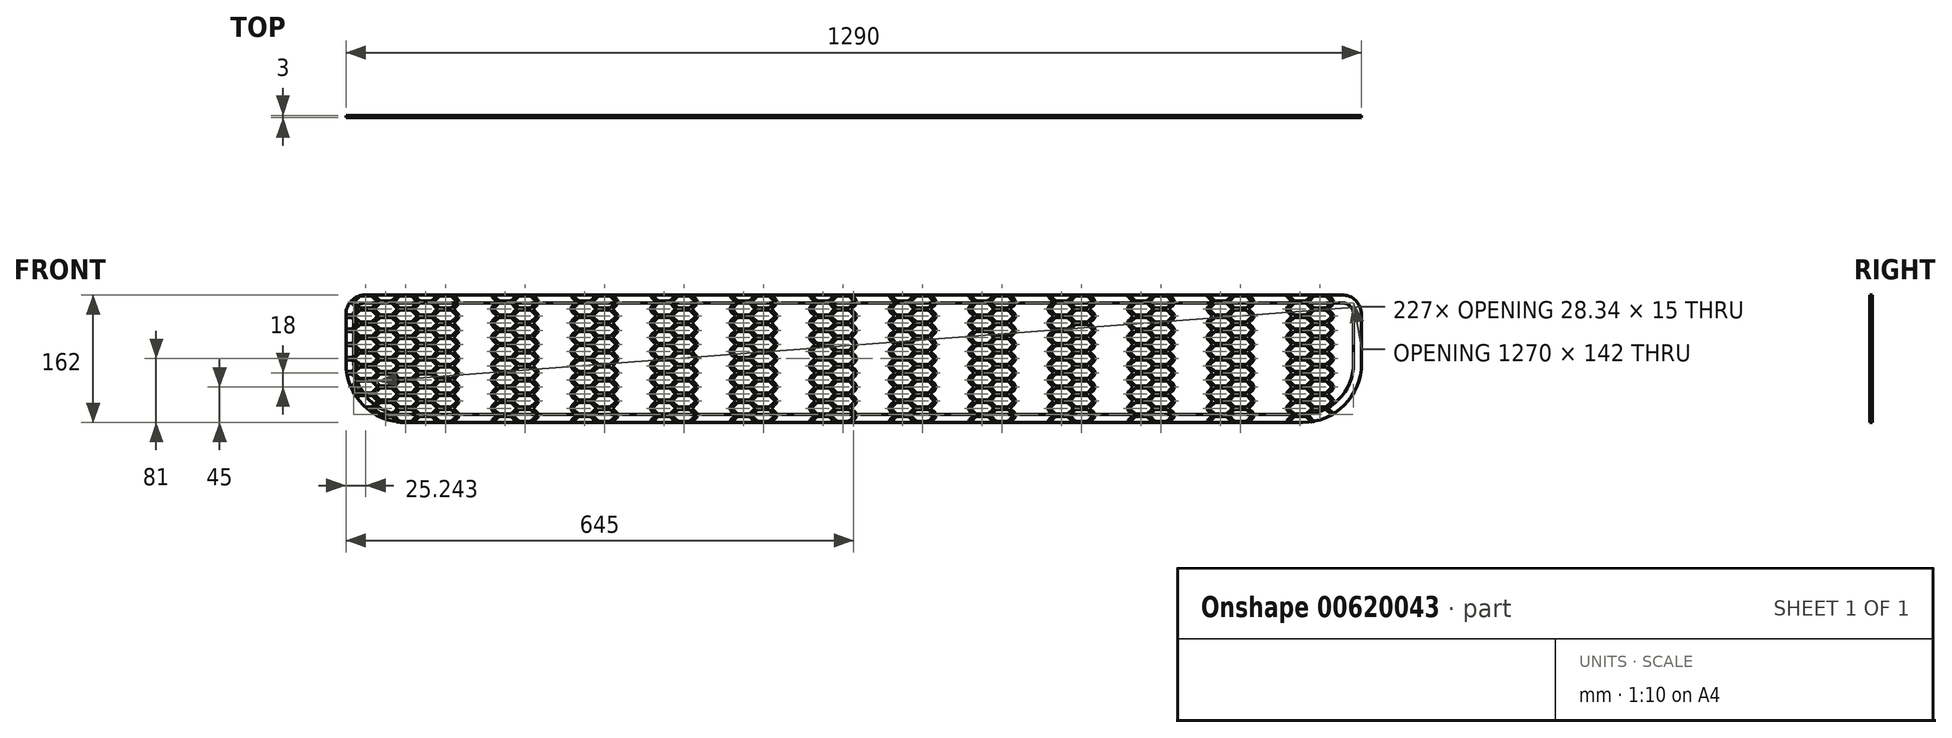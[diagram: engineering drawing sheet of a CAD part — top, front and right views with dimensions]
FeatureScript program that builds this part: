
annotation { "Feature Type Name" : "Feature", "Feature Type Description" : "" }
export const myFeature = defineFeature(function(context is Context, id is Id, definition is map)
    precondition{}
    {
        {
            var Q0;
            Q0=qCreatedBy(makeId("Front.planeOp"),FACE);
            var sketch = newSketch(context, id + "F0", { "sketchPlane" : qUnion([Q0])});
            skLineSegment(sketch, "E0.bottom", {"start": v(6.67, -7.5) * mm, "end": v(-6.67, -7.5) * mm});
            skLineSegment(sketch, "E0.top", {"start": v(6.67, 7.5) * mm, "end": v(-6.67, 7.5) * mm});
            skPoint(sketch, "E0.middle", {"position": v(0, 0) * mm});
            skLineSegment(sketch, "E1", {"start": v(-8.09, 6.91) * mm, "end": v(-13.59, 1.41) * mm});
            skLineSegment(sketch, "E2", {"start": v(-8.09, -6.91) * mm, "end": v(-13.59, -1.41) * mm});
            skLineSegment(sketch, "E3", {"start": v(8.09, 6.91) * mm, "end": v(13.59, 1.41) * mm});
            skLineSegment(sketch, "E4", {"start": v(13.59, -1.41) * mm, "end": v(8.09, -6.91) * mm});
            skPoint(sketch, "E5.visualSharp", {"position": v(-15, 0) * mm});
            skArc(sketch, "E5.filletArc", {"start": v(-13.59, 1.41) * mm, "mid": v(-14.17, 0) * mm, "end": v(-13.59, -1.41) * mm});
            skPoint(sketch, "E6.visualSharp", {"position": v(15, 0) * mm});
            skArc(sketch, "E6.filletArc", {"start": v(13.59, -1.41) * mm, "mid": v(14.17, 0) * mm, "end": v(13.59, 1.41) * mm});
            skPoint(sketch, "E7.visualSharp", {"position": v(7.5, -7.5) * mm});
            skArc(sketch, "E7.filletArc", {"start": v(6.67, -7.5) * mm, "mid": v(7.44, -7.35) * mm, "end": v(8.09, -6.91) * mm});
            skPoint(sketch, "E8.visualSharp", {"position": v(-7.5, -7.5) * mm});
            skArc(sketch, "E8.filletArc", {"start": v(-8.09, -6.91) * mm, "mid": v(-7.44, -7.35) * mm, "end": v(-6.67, -7.5) * mm});
            skArc(sketch, "E9.filletArc", {"start": v(-6.67, 7.5) * mm, "mid": v(-7.44, 7.35) * mm, "end": v(-8.09, 6.91) * mm});
            skArc(sketch, "E10.filletArc", {"start": v(8.09, 6.91) * mm, "mid": v(7.44, 7.35) * mm, "end": v(6.67, 7.5) * mm});
            skLineSegment(sketch, "E11.0.7.2", {"start": v(17.16, 160.1) * mm, "end": v(11.66, 154.6) * mm});
            skLineSegment(sketch, "E11.0.7.3", {"start": v(31.91, 160.68) * mm, "end": v(18.57, 160.68) * mm});
            skLineSegment(sketch, "E11.0.7.5", {"start": v(33.33, 160.1) * mm, "end": v(38.83, 154.6) * mm});
            skArc(sketch, "E11.0.7.7", {"start": v(33.33, 160.1) * mm, "mid": v(32.68, 160.53) * mm, "end": v(31.91, 160.68) * mm});
            skArc(sketch, "E11.0.7.10", {"start": v(18.57, 160.68) * mm, "mid": v(17.8, 160.53) * mm, "end": v(17.16, 160.1) * mm});
            skArc(sketch, "E12.0", {"start": v(10.2, 9.04) * mm, "mid": v(8.58, 10.12) * mm, "end": v(6.67, 10.5) * mm});
            skLineSegment(sketch, "E12.1", {"start": v(-10.2, -9.04) * mm, "end": v(-15.7, -3.54) * mm});
            skArc(sketch, "E12.2", {"start": v(-15.7, 3.54) * mm, "mid": v(-17.17, 0) * mm, "end": v(-15.7, -3.54) * mm});
            skLineSegment(sketch, "E12.3", {"start": v(-10.2, 9.04) * mm, "end": v(-15.7, 3.54) * mm});
            skArc(sketch, "E12.4", {"start": v(-6.67, 10.5) * mm, "mid": v(-8.58, 10.12) * mm, "end": v(-10.2, 9.04) * mm});
            skArc(sketch, "E12.5", {"start": v(-10.2, -9.04) * mm, "mid": v(-8.58, -10.12) * mm, "end": v(-6.67, -10.5) * mm});
            skLineSegment(sketch, "E12.6", {"start": v(6.67, 10.5) * mm, "end": v(-6.67, 10.5) * mm});
            skLineSegment(sketch, "E12.7", {"start": v(6.67, -10.5) * mm, "end": v(-6.67, -10.5) * mm});
            skArc(sketch, "E12.8", {"start": v(6.67, -10.5) * mm, "mid": v(8.58, -10.12) * mm, "end": v(10.2, -9.04) * mm});
            skLineSegment(sketch, "E12.9", {"start": v(15.7, -3.54) * mm, "end": v(10.2, -9.04) * mm});
            skArc(sketch, "E12.10", {"start": v(15.7, -3.54) * mm, "mid": v(17.17, 0) * mm, "end": v(15.7, 3.54) * mm});
            skLineSegment(sketch, "E12.11", {"start": v(10.2, 9.04) * mm, "end": v(15.7, 3.54) * mm});
            skLineSegment(sketch, "E13.bottom", {"start": v(-6.67, 5.5) * mm, "end": v(6.67, 5.5) * mm, "construction": true});
            skLineSegment(sketch, "E13.top", {"start": v(-6.67, -5.5) * mm, "end": v(6.67, -5.5) * mm, "construction": true});
            skLineSegment(sketch, "E13.left", {"start": v(-6.67, 5.5) * mm, "end": v(-6.67, -5.5) * mm, "construction": true});
            skLineSegment(sketch, "E13.right", {"start": v(6.67, 5.5) * mm, "end": v(6.67, -5.5) * mm, "construction": true});
            skSolve(sketch);
        }
        {
            var Q0;
            Q0=makeQuery(id+"F0.imprint","IMPRINT",FACE,{"disambiguationData":[TD([[makeQuery(id+"F0.imprint","IMPRINT",EDGE,{"derivedFrom":sQuery(id+"F0.wireOp",EDGE,"E0.bottom")}),1.0]])]});
            extrude(context, id + "F1", {"entities" : qUnion([Q0]), "depth" : 3 * mm, "offsetDistance" : 25 * mm});
        }
        {
            var Q0;
            Q0=qCreatedBy(makeId("Front.planeOp"),FACE);
            var sketch = newSketch(context, id + "F2", { "sketchPlane" : qUnion([Q0])});
            skLineSegment(sketch, "E14.0", {"start": v(6.67, -7.5) * mm, "end": v(-6.67, -7.5) * mm});
            skLineSegment(sketch, "E15.bottom", {"start": v(6.67, -25.5) * mm, "end": v(-6.67, -25.5) * mm});
            skLineSegment(sketch, "E15.top", {"start": v(6.67, -10.5) * mm, "end": v(-6.67, -10.5) * mm});
            skPoint(sketch, "E15.middle", {"position": v(0, -18) * mm});
            skLineSegment(sketch, "E16", {"start": v(-8.09, -11.09) * mm, "end": v(-13.59, -16.59) * mm});
            skLineSegment(sketch, "E17", {"start": v(-8.09, -24.91) * mm, "end": v(-13.59, -19.41) * mm});
            skLineSegment(sketch, "E18", {"start": v(8.09, -11.09) * mm, "end": v(13.59, -16.59) * mm});
            skLineSegment(sketch, "E19", {"start": v(13.59, -19.41) * mm, "end": v(8.09, -24.91) * mm});
            skPoint(sketch, "E20.visualSharp", {"position": v(-15, -18) * mm});
            skArc(sketch, "E20.filletArc", {"start": v(-13.59, -16.59) * mm, "mid": v(-14.17, -18) * mm, "end": v(-13.59, -19.41) * mm});
            skPoint(sketch, "E21.visualSharp", {"position": v(15, -18) * mm});
            skArc(sketch, "E21.filletArc", {"start": v(13.59, -19.41) * mm, "mid": v(14.17, -18) * mm, "end": v(13.59, -16.59) * mm});
            skPoint(sketch, "E22.visualSharp", {"position": v(7.5, -25.5) * mm});
            skArc(sketch, "E22.filletArc", {"start": v(6.67, -25.5) * mm, "mid": v(7.44, -25.35) * mm, "end": v(8.09, -24.91) * mm});
            skPoint(sketch, "E23.visualSharp", {"position": v(-7.5, -25.5) * mm});
            skArc(sketch, "E23.filletArc", {"start": v(-8.09, -24.91) * mm, "mid": v(-7.44, -25.35) * mm, "end": v(-6.67, -25.5) * mm});
            skArc(sketch, "E24.filletArc", {"start": v(-6.67, -10.5) * mm, "mid": v(-7.44, -10.65) * mm, "end": v(-8.09, -11.09) * mm});
            skArc(sketch, "E25.filletArc", {"start": v(8.09, -11.09) * mm, "mid": v(7.44, -10.65) * mm, "end": v(6.67, -10.5) * mm});
            skArc(sketch, "E26.0", {"start": v(10.2, -8.96) * mm, "mid": v(8.58, -7.88) * mm, "end": v(6.67, -7.5) * mm});
            skLineSegment(sketch, "E26.1", {"start": v(-10.2, -27.04) * mm, "end": v(-15.7, -21.54) * mm});
            skArc(sketch, "E26.2", {"start": v(-15.7, -14.46) * mm, "mid": v(-17.17, -18) * mm, "end": v(-15.7, -21.54) * mm});
            skLineSegment(sketch, "E26.3", {"start": v(-10.2, -8.96) * mm, "end": v(-15.7, -14.46) * mm});
            skArc(sketch, "E26.4", {"start": v(-6.67, -7.5) * mm, "mid": v(-8.58, -7.88) * mm, "end": v(-10.2, -8.96) * mm});
            skArc(sketch, "E26.5", {"start": v(-10.2, -27.04) * mm, "mid": v(-8.58, -28.12) * mm, "end": v(-6.67, -28.5) * mm});
            skLineSegment(sketch, "E26.7", {"start": v(6.67, -28.5) * mm, "end": v(-6.67, -28.5) * mm});
            skArc(sketch, "E26.8", {"start": v(6.67, -28.5) * mm, "mid": v(8.58, -28.12) * mm, "end": v(10.2, -27.04) * mm});
            skLineSegment(sketch, "E26.9", {"start": v(15.7, -21.54) * mm, "end": v(10.2, -27.04) * mm});
            skArc(sketch, "E26.10", {"start": v(15.7, -21.54) * mm, "mid": v(17.17, -18) * mm, "end": v(15.7, -14.46) * mm});
            skLineSegment(sketch, "E26.11", {"start": v(10.2, -8.96) * mm, "end": v(15.7, -14.46) * mm});
            skLineSegment(sketch, "E27.bottom", {"start": v(-6.67, -12.5) * mm, "end": v(6.67, -12.5) * mm, "construction": true});
            skLineSegment(sketch, "E27.top", {"start": v(-6.67, -23.5) * mm, "end": v(6.67, -23.5) * mm, "construction": true});
            skLineSegment(sketch, "E27.left", {"start": v(-6.67, -12.5) * mm, "end": v(-6.67, -23.5) * mm, "construction": true});
            skLineSegment(sketch, "E27.right", {"start": v(6.67, -12.5) * mm, "end": v(6.67, -23.5) * mm, "construction": true});
            skSolve(sketch);
        }
        {
            var Q0;
            Q0=makeQuery(id+"F2.imprint","IMPRINT",FACE,{"disambiguationData":[TD([[makeQuery(id+"F2.imprint","IMPRINT",EDGE,{"derivedFrom":sQuery(id+"F2.wireOp",EDGE,"E15.bottom")}),1.0]])]});
            extrude(context, id + "F3", {"entities" : qUnion([Q0]), "operationType" : NewBodyOperationType.ADD, "depth" : 3 * mm, "offsetDistance" : 25 * mm});
        }
        {
            var Q0;
            Q0=qCreatedBy(makeId("Front.planeOp"),FACE);
            var sketch = newSketch(context, id + "F4", { "sketchPlane" : qUnion([Q0])});
            skLineSegment(sketch, "E28.bottom", {"start": v(64.28, 40.04) * mm, "end": v(50.94, 40.04) * mm});
            skLineSegment(sketch, "E28.top", {"start": v(64.28, 55.04) * mm, "end": v(50.94, 55.04) * mm});
            skPoint(sketch, "E28.middle", {"position": v(57.61, 47.54) * mm});
            skLineSegment(sketch, "E29", {"start": v(49.53, 54.45) * mm, "end": v(44.03, 48.95) * mm});
            skLineSegment(sketch, "E30", {"start": v(49.53, 40.62) * mm, "end": v(44.03, 46.12) * mm});
            skLineSegment(sketch, "E31", {"start": v(65.7, 54.45) * mm, "end": v(71.2, 48.95) * mm});
            skLineSegment(sketch, "E32", {"start": v(71.2, 46.12) * mm, "end": v(65.7, 40.62) * mm});
            skPoint(sketch, "E33.visualSharp", {"position": v(42.61, 47.54) * mm});
            skArc(sketch, "E33.filletArc", {"start": v(44.03, 48.95) * mm, "mid": v(43.44, 47.54) * mm, "end": v(44.03, 46.12) * mm});
            skPoint(sketch, "E34.visualSharp", {"position": v(72.61, 47.54) * mm});
            skArc(sketch, "E34.filletArc", {"start": v(71.2, 46.12) * mm, "mid": v(71.78, 47.54) * mm, "end": v(71.2, 48.95) * mm});
            skPoint(sketch, "E35.visualSharp", {"position": v(65.11, 40.04) * mm});
            skArc(sketch, "E35.filletArc", {"start": v(64.28, 40.04) * mm, "mid": v(65.05, 40.2) * mm, "end": v(65.7, 40.62) * mm});
            skPoint(sketch, "E36.visualSharp", {"position": v(50.11, 40.04) * mm});
            skArc(sketch, "E36.filletArc", {"start": v(49.53, 40.62) * mm, "mid": v(50.18, 40.2) * mm, "end": v(50.94, 40.04) * mm});
            skArc(sketch, "E37.filletArc", {"start": v(50.94, 55.04) * mm, "mid": v(50.18, 54.89) * mm, "end": v(49.53, 54.45) * mm});
            skArc(sketch, "E38.filletArc", {"start": v(65.7, 54.45) * mm, "mid": v(65.05, 54.89) * mm, "end": v(64.28, 55.04) * mm});
            skArc(sketch, "E39.0", {"start": v(67.82, 56.57) * mm, "mid": v(66.2, 57.66) * mm, "end": v(64.28, 58.04) * mm});
            skLineSegment(sketch, "E39.1", {"start": v(47.4, 38.5) * mm, "end": v(41.9, 44) * mm});
            skArc(sketch, "E39.2", {"start": v(41.9, 51.07) * mm, "mid": v(40.44, 47.54) * mm, "end": v(41.9, 44) * mm});
            skLineSegment(sketch, "E39.3", {"start": v(47.4, 56.57) * mm, "end": v(41.9, 51.07) * mm});
            skArc(sketch, "E39.4", {"start": v(50.94, 58.04) * mm, "mid": v(49.03, 57.66) * mm, "end": v(47.4, 56.57) * mm});
            skArc(sketch, "E39.5", {"start": v(47.4, 38.5) * mm, "mid": v(49.03, 37.42) * mm, "end": v(50.94, 37.04) * mm});
            skLineSegment(sketch, "E39.6", {"start": v(64.28, 58.04) * mm, "end": v(50.94, 58.04) * mm});
            skLineSegment(sketch, "E39.7", {"start": v(64.28, 37.04) * mm, "end": v(50.94, 37.04) * mm});
            skArc(sketch, "E39.8", {"start": v(64.28, 37.04) * mm, "mid": v(66.2, 37.42) * mm, "end": v(67.82, 38.5) * mm});
            skLineSegment(sketch, "E39.9", {"start": v(73.32, 44) * mm, "end": v(67.82, 38.5) * mm});
            skArc(sketch, "E39.10", {"start": v(73.32, 44) * mm, "mid": v(74.78, 47.54) * mm, "end": v(73.32, 51.07) * mm});
            skLineSegment(sketch, "E39.11", {"start": v(67.82, 56.57) * mm, "end": v(73.32, 51.07) * mm});
            skLineSegment(sketch, "E40.bottom", {"start": v(50.94, 53.04) * mm, "end": v(64.28, 53.04) * mm, "construction": true});
            skLineSegment(sketch, "E40.top", {"start": v(50.94, 42.04) * mm, "end": v(64.28, 42.04) * mm, "construction": true});
            skLineSegment(sketch, "E40.left", {"start": v(50.94, 53.04) * mm, "end": v(50.94, 42.04) * mm, "construction": true});
            skLineSegment(sketch, "E40.right", {"start": v(64.28, 53.04) * mm, "end": v(64.28, 42.04) * mm, "construction": true});
            skLineSegment(sketch, "E41.0", {"start": v(15.7, -3.54) * mm, "end": v(10.24, -9) * mm});
            skLineSegment(sketch, "E42.bottom", {"start": v(31.91, -16.5) * mm, "end": v(18.57, -16.5) * mm});
            skLineSegment(sketch, "E42.top", {"start": v(31.91, -1.5) * mm, "end": v(18.57, -1.5) * mm});
            skPoint(sketch, "E42.middle", {"position": v(25.24, -9) * mm});
            skLineSegment(sketch, "E43", {"start": v(17.16, -2.09) * mm, "end": v(11.66, -7.59) * mm});
            skLineSegment(sketch, "E44", {"start": v(17.16, -15.91) * mm, "end": v(11.66, -10.41) * mm});
            skLineSegment(sketch, "E45", {"start": v(33.33, -2.09) * mm, "end": v(38.83, -7.59) * mm});
            skLineSegment(sketch, "E46", {"start": v(38.83, -10.41) * mm, "end": v(33.33, -15.91) * mm});
            skPoint(sketch, "E47.visualSharp", {"position": v(10.24, -9) * mm});
            skArc(sketch, "E47.filletArc", {"start": v(11.66, -7.59) * mm, "mid": v(11.07, -9) * mm, "end": v(11.66, -10.41) * mm});
            skPoint(sketch, "E48.visualSharp", {"position": v(40.24, -9) * mm});
            skArc(sketch, "E48.filletArc", {"start": v(38.83, -10.41) * mm, "mid": v(39.41, -9) * mm, "end": v(38.83, -7.59) * mm});
            skPoint(sketch, "E49.visualSharp", {"position": v(32.74, -16.5) * mm});
            skArc(sketch, "E49.filletArc", {"start": v(31.91, -16.5) * mm, "mid": v(32.68, -16.35) * mm, "end": v(33.33, -15.91) * mm});
            skPoint(sketch, "E50.visualSharp", {"position": v(17.74, -16.5) * mm});
            skArc(sketch, "E50.filletArc", {"start": v(17.16, -15.91) * mm, "mid": v(17.8, -16.35) * mm, "end": v(18.57, -16.5) * mm});
            skArc(sketch, "E51.filletArc", {"start": v(18.57, -1.5) * mm, "mid": v(17.8, -1.65) * mm, "end": v(17.16, -2.09) * mm});
            skArc(sketch, "E52.filletArc", {"start": v(33.33, -2.09) * mm, "mid": v(32.68, -1.65) * mm, "end": v(31.91, -1.5) * mm});
            skArc(sketch, "E53.0", {"start": v(35.45, 0.04) * mm, "mid": v(33.83, 1.12) * mm, "end": v(31.91, 1.5) * mm});
            skLineSegment(sketch, "E53.1", {"start": v(15.04, -18.04) * mm, "end": v(9.54, -12.54) * mm});
            skArc(sketch, "E53.2", {"start": v(9.54, -5.46) * mm, "mid": v(8.07, -9) * mm, "end": v(9.54, -12.54) * mm});
            skLineSegment(sketch, "E53.3", {"start": v(15.04, 0.04) * mm, "end": v(9.54, -5.46) * mm});
            skArc(sketch, "E53.4", {"start": v(18.57, 1.5) * mm, "mid": v(16.66, 1.12) * mm, "end": v(15.04, 0.04) * mm});
            skArc(sketch, "E53.5", {"start": v(15.04, -18.04) * mm, "mid": v(16.66, -19.12) * mm, "end": v(18.57, -19.5) * mm});
            skLineSegment(sketch, "E53.6", {"start": v(31.91, 1.5) * mm, "end": v(18.57, 1.5) * mm});
            skLineSegment(sketch, "E53.7", {"start": v(31.91, -19.5) * mm, "end": v(18.57, -19.5) * mm});
            skArc(sketch, "E53.8", {"start": v(31.91, -19.5) * mm, "mid": v(33.83, -19.12) * mm, "end": v(35.45, -18.04) * mm});
            skLineSegment(sketch, "E53.9", {"start": v(40.95, -12.54) * mm, "end": v(35.45, -18.04) * mm});
            skArc(sketch, "E53.10", {"start": v(40.95, -12.54) * mm, "mid": v(42.41, -9) * mm, "end": v(40.95, -5.46) * mm});
            skLineSegment(sketch, "E53.11", {"start": v(35.45, 0.04) * mm, "end": v(40.95, -5.46) * mm});
            skLineSegment(sketch, "E54.bottom", {"start": v(18.57, -3.5) * mm, "end": v(31.91, -3.5) * mm, "construction": true});
            skLineSegment(sketch, "E54.top", {"start": v(18.57, -14.5) * mm, "end": v(31.91, -14.5) * mm, "construction": true});
            skLineSegment(sketch, "E54.left", {"start": v(18.57, -3.5) * mm, "end": v(18.57, -14.5) * mm, "construction": true});
            skLineSegment(sketch, "E54.right", {"start": v(31.91, -3.5) * mm, "end": v(31.91, -14.5) * mm, "construction": true});
            skSolve(sketch);
        }
        {
            var Q0;
            Q0=makeQuery(id+"F4.imprint","IMPRINT",FACE,{"disambiguationData":[TD([[makeQuery(id+"F4.imprint","IMPRINT",EDGE,{"derivedFrom":sQuery(id+"F4.wireOp",EDGE,"E42.bottom")}),1.0]])]});
            extrude(context, id + "F5", {"entities" : qUnion([Q0]), "operationType" : NewBodyOperationType.ADD, "depth" : 3 * mm, "offsetDistance" : 25 * mm});
        }
        {
            var Q0;
            Q0=qCreatedBy(makeId("Front.planeOp"),FACE);
            var sketch = newSketch(context, id + "F6", { "sketchPlane" : qUnion([Q0])});
            skLineSegment(sketch, "E55.0", {"start": v(31.91, -1.5) * mm, "end": v(18.57, -1.5) * mm});
            skLineSegment(sketch, "E56.bottom", {"start": v(31.91, 1.5) * mm, "end": v(18.57, 1.5) * mm});
            skLineSegment(sketch, "E56.top", {"start": v(31.91, 16.5) * mm, "end": v(18.57, 16.5) * mm});
            skPoint(sketch, "E56.middle", {"position": v(25.24, 9) * mm});
            skLineSegment(sketch, "E57", {"start": v(17.16, 15.91) * mm, "end": v(11.66, 10.41) * mm});
            skLineSegment(sketch, "E58", {"start": v(17.16, 2.09) * mm, "end": v(11.66, 7.59) * mm});
            skLineSegment(sketch, "E59", {"start": v(33.33, 15.91) * mm, "end": v(38.83, 10.41) * mm});
            skLineSegment(sketch, "E60", {"start": v(38.83, 7.59) * mm, "end": v(33.33, 2.09) * mm});
            skPoint(sketch, "E61.visualSharp", {"position": v(10.24, 9) * mm});
            skArc(sketch, "E61.filletArc", {"start": v(11.66, 10.41) * mm, "mid": v(11.07, 9) * mm, "end": v(11.66, 7.59) * mm});
            skPoint(sketch, "E62.visualSharp", {"position": v(40.24, 9) * mm});
            skArc(sketch, "E62.filletArc", {"start": v(38.83, 7.59) * mm, "mid": v(39.41, 9) * mm, "end": v(38.83, 10.41) * mm});
            skPoint(sketch, "E63.visualSharp", {"position": v(32.74, 1.5) * mm});
            skArc(sketch, "E63.filletArc", {"start": v(31.91, 1.5) * mm, "mid": v(32.68, 1.65) * mm, "end": v(33.33, 2.09) * mm});
            skPoint(sketch, "E64.visualSharp", {"position": v(17.74, 1.5) * mm});
            skArc(sketch, "E64.filletArc", {"start": v(17.16, 2.09) * mm, "mid": v(17.8, 1.65) * mm, "end": v(18.57, 1.5) * mm});
            skArc(sketch, "E65.filletArc", {"start": v(18.57, 16.5) * mm, "mid": v(17.8, 16.35) * mm, "end": v(17.16, 15.91) * mm});
            skArc(sketch, "E66.filletArc", {"start": v(33.33, 15.91) * mm, "mid": v(32.68, 16.35) * mm, "end": v(31.91, 16.5) * mm});
            skArc(sketch, "E67.0", {"start": v(35.45, 18.04) * mm, "mid": v(33.83, 19.12) * mm, "end": v(31.91, 19.5) * mm});
            skLineSegment(sketch, "E67.1", {"start": v(15.04, -0.04) * mm, "end": v(9.54, 5.46) * mm});
            skArc(sketch, "E67.2", {"start": v(9.54, 12.54) * mm, "mid": v(8.07, 9) * mm, "end": v(9.54, 5.46) * mm});
            skLineSegment(sketch, "E67.3", {"start": v(15.04, 18.04) * mm, "end": v(9.54, 12.54) * mm});
            skArc(sketch, "E67.4", {"start": v(18.57, 19.5) * mm, "mid": v(16.66, 19.12) * mm, "end": v(15.04, 18.04) * mm});
            skArc(sketch, "E67.5", {"start": v(15.04, -0.04) * mm, "mid": v(16.66, -1.12) * mm, "end": v(18.57, -1.5) * mm});
            skLineSegment(sketch, "E67.6", {"start": v(31.91, 19.5) * mm, "end": v(18.57, 19.5) * mm});
            skArc(sketch, "E67.8", {"start": v(31.91, -1.5) * mm, "mid": v(33.83, -1.12) * mm, "end": v(35.45, -0.04) * mm});
            skLineSegment(sketch, "E67.9", {"start": v(40.95, 5.46) * mm, "end": v(35.45, -0.04) * mm});
            skArc(sketch, "E67.10", {"start": v(40.95, 5.46) * mm, "mid": v(42.41, 9) * mm, "end": v(40.95, 12.54) * mm});
            skLineSegment(sketch, "E67.11", {"start": v(35.45, 18.04) * mm, "end": v(40.95, 12.54) * mm});
            skLineSegment(sketch, "E68.bottom", {"start": v(18.57, 14.5) * mm, "end": v(31.91, 14.5) * mm, "construction": true});
            skLineSegment(sketch, "E68.top", {"start": v(18.57, 3.5) * mm, "end": v(31.91, 3.5) * mm, "construction": true});
            skLineSegment(sketch, "E68.left", {"start": v(18.57, 14.5) * mm, "end": v(18.57, 3.5) * mm, "construction": true});
            skLineSegment(sketch, "E68.right", {"start": v(31.91, 14.5) * mm, "end": v(31.91, 3.5) * mm, "construction": true});
            skSolve(sketch);
        }
        {
            var Q0;
            Q0=makeQuery(id+"F6.imprint","IMPRINT",FACE,{"disambiguationData":[TD([[makeQuery(id+"F6.imprint","IMPRINT",EDGE,{"derivedFrom":sQuery(id+"F6.wireOp",EDGE,"E56.bottom")}),1.0]])]});
            extrude(context, id + "F7", {"entities" : qUnion([Q0]), "operationType" : NewBodyOperationType.ADD, "depth" : 3 * mm, "offsetDistance" : 25 * mm});
        }
        {
            var Q0;
            Q0=makeQuery(id+"F1.opExtrude","SWEPT_BODY",BODY,{"disambiguationData":[OSD([sQuery(id+"F0.wireOp",EDGE,"E0.bottom"),sQuery(id+"F0.wireOp",EDGE,"E0.top"),sQuery(id+"F0.wireOp",EDGE,"E1"),sQuery(id+"F0.wireOp",EDGE,"E2"),sQuery(id+"F0.wireOp",EDGE,"E3"),sQuery(id+"F0.wireOp",EDGE,"E4"),sQuery(id+"F0.wireOp",EDGE,"E5.filletArc"),sQuery(id+"F0.wireOp",EDGE,"E6.filletArc"),sQuery(id+"F0.wireOp",EDGE,"E7.filletArc"),sQuery(id+"F0.wireOp",EDGE,"E8.filletArc"),sQuery(id+"F0.wireOp",EDGE,"E9.filletArc"),sQuery(id+"F0.wireOp",EDGE,"E10.filletArc"),sQuery(id+"F0.wireOp",EDGE,"E12.0"),sQuery(id+"F0.wireOp",EDGE,"E12.1"),sQuery(id+"F0.wireOp",EDGE,"E12.2"),sQuery(id+"F0.wireOp",EDGE,"E12.3"),sQuery(id+"F0.wireOp",EDGE,"E12.4"),sQuery(id+"F0.wireOp",EDGE,"E12.5"),sQuery(id+"F0.wireOp",EDGE,"E12.6"),sQuery(id+"F0.wireOp",EDGE,"E12.7"),sQuery(id+"F0.wireOp",EDGE,"E12.8"),sQuery(id+"F0.wireOp",EDGE,"E12.9"),sQuery(id+"F0.wireOp",EDGE,"E12.10"),sQuery(id+"F0.wireOp",EDGE,"E12.11")])]});
            transform(context, id + "F8", {"entities" : qUnion([Q0]), "transformType" : TransformType.TRANSLATION_3D, "dx" : 0 * mm, "dy" : 0 * mm, "dz" : 36 * mm, "makeCopy" : true});
        }
        {
            var Q0;
            Q0=makeQuery(id+"F8.opPattern","COPY",BODY,{"derivedFrom":makeQuery(id+"F1.opExtrude","SWEPT_BODY",BODY,{"disambiguationData":[OSD([sQuery(id+"F0.wireOp",EDGE,"E0.bottom"),sQuery(id+"F0.wireOp",EDGE,"E0.top"),sQuery(id+"F0.wireOp",EDGE,"E1"),sQuery(id+"F0.wireOp",EDGE,"E2"),sQuery(id+"F0.wireOp",EDGE,"E3"),sQuery(id+"F0.wireOp",EDGE,"E4"),sQuery(id+"F0.wireOp",EDGE,"E5.filletArc"),sQuery(id+"F0.wireOp",EDGE,"E6.filletArc"),sQuery(id+"F0.wireOp",EDGE,"E7.filletArc"),sQuery(id+"F0.wireOp",EDGE,"E8.filletArc"),sQuery(id+"F0.wireOp",EDGE,"E9.filletArc"),sQuery(id+"F0.wireOp",EDGE,"E10.filletArc"),sQuery(id+"F0.wireOp",EDGE,"E12.0"),sQuery(id+"F0.wireOp",EDGE,"E12.1"),sQuery(id+"F0.wireOp",EDGE,"E12.2"),sQuery(id+"F0.wireOp",EDGE,"E12.3"),sQuery(id+"F0.wireOp",EDGE,"E12.4"),sQuery(id+"F0.wireOp",EDGE,"E12.5"),sQuery(id+"F0.wireOp",EDGE,"E12.6"),sQuery(id+"F0.wireOp",EDGE,"E12.7"),sQuery(id+"F0.wireOp",EDGE,"E12.8"),sQuery(id+"F0.wireOp",EDGE,"E12.9"),sQuery(id+"F0.wireOp",EDGE,"E12.10"),sQuery(id+"F0.wireOp",EDGE,"E12.11")])]}),"instanceName":"1"});
            transform(context, id + "F9", {"entities" : qUnion([Q0]), "transformType" : TransformType.TRANSLATION_3D, "dx" : 0 * mm, "dy" : 0 * mm, "dz" : 36 * mm, "makeCopy" : true});
        }
        {
            var Q0;
            Q0=makeQuery(id+"F1.opExtrude","SWEPT_BODY",BODY,{"disambiguationData":[OSD([sQuery(id+"F0.wireOp",EDGE,"E0.bottom"),sQuery(id+"F0.wireOp",EDGE,"E0.top"),sQuery(id+"F0.wireOp",EDGE,"E1"),sQuery(id+"F0.wireOp",EDGE,"E2"),sQuery(id+"F0.wireOp",EDGE,"E3"),sQuery(id+"F0.wireOp",EDGE,"E4"),sQuery(id+"F0.wireOp",EDGE,"E5.filletArc"),sQuery(id+"F0.wireOp",EDGE,"E6.filletArc"),sQuery(id+"F0.wireOp",EDGE,"E7.filletArc"),sQuery(id+"F0.wireOp",EDGE,"E8.filletArc"),sQuery(id+"F0.wireOp",EDGE,"E9.filletArc"),sQuery(id+"F0.wireOp",EDGE,"E10.filletArc"),sQuery(id+"F0.wireOp",EDGE,"E12.0"),sQuery(id+"F0.wireOp",EDGE,"E12.1"),sQuery(id+"F0.wireOp",EDGE,"E12.2"),sQuery(id+"F0.wireOp",EDGE,"E12.3"),sQuery(id+"F0.wireOp",EDGE,"E12.4"),sQuery(id+"F0.wireOp",EDGE,"E12.5"),sQuery(id+"F0.wireOp",EDGE,"E12.6"),sQuery(id+"F0.wireOp",EDGE,"E12.7"),sQuery(id+"F0.wireOp",EDGE,"E12.8"),sQuery(id+"F0.wireOp",EDGE,"E12.9"),sQuery(id+"F0.wireOp",EDGE,"E12.10"),sQuery(id+"F0.wireOp",EDGE,"E12.11")])]});
            var Q1;
            Q1=makeQuery(id+"F8.opPattern","COPY",BODY,{"derivedFrom":makeQuery(id+"F1.opExtrude","SWEPT_BODY",BODY,{"disambiguationData":[OSD([sQuery(id+"F0.wireOp",EDGE,"E0.bottom"),sQuery(id+"F0.wireOp",EDGE,"E0.top"),sQuery(id+"F0.wireOp",EDGE,"E1"),sQuery(id+"F0.wireOp",EDGE,"E2"),sQuery(id+"F0.wireOp",EDGE,"E3"),sQuery(id+"F0.wireOp",EDGE,"E4"),sQuery(id+"F0.wireOp",EDGE,"E5.filletArc"),sQuery(id+"F0.wireOp",EDGE,"E6.filletArc"),sQuery(id+"F0.wireOp",EDGE,"E7.filletArc"),sQuery(id+"F0.wireOp",EDGE,"E8.filletArc"),sQuery(id+"F0.wireOp",EDGE,"E9.filletArc"),sQuery(id+"F0.wireOp",EDGE,"E10.filletArc"),sQuery(id+"F0.wireOp",EDGE,"E12.0"),sQuery(id+"F0.wireOp",EDGE,"E12.1"),sQuery(id+"F0.wireOp",EDGE,"E12.2"),sQuery(id+"F0.wireOp",EDGE,"E12.3"),sQuery(id+"F0.wireOp",EDGE,"E12.4"),sQuery(id+"F0.wireOp",EDGE,"E12.5"),sQuery(id+"F0.wireOp",EDGE,"E12.6"),sQuery(id+"F0.wireOp",EDGE,"E12.7"),sQuery(id+"F0.wireOp",EDGE,"E12.8"),sQuery(id+"F0.wireOp",EDGE,"E12.9"),sQuery(id+"F0.wireOp",EDGE,"E12.10"),sQuery(id+"F0.wireOp",EDGE,"E12.11")])]}),"instanceName":"1"});
            var Q2;
            Q2=makeQuery(id+"F9.opPattern","COPY",BODY,{"derivedFrom":makeQuery(id+"F8.opPattern","COPY",BODY,{"derivedFrom":makeQuery(id+"F1.opExtrude","SWEPT_BODY",BODY,{"disambiguationData":[OSD([sQuery(id+"F0.wireOp",EDGE,"E0.bottom"),sQuery(id+"F0.wireOp",EDGE,"E0.top"),sQuery(id+"F0.wireOp",EDGE,"E1"),sQuery(id+"F0.wireOp",EDGE,"E2"),sQuery(id+"F0.wireOp",EDGE,"E3"),sQuery(id+"F0.wireOp",EDGE,"E4"),sQuery(id+"F0.wireOp",EDGE,"E5.filletArc"),sQuery(id+"F0.wireOp",EDGE,"E6.filletArc"),sQuery(id+"F0.wireOp",EDGE,"E7.filletArc"),sQuery(id+"F0.wireOp",EDGE,"E8.filletArc"),sQuery(id+"F0.wireOp",EDGE,"E9.filletArc"),sQuery(id+"F0.wireOp",EDGE,"E10.filletArc"),sQuery(id+"F0.wireOp",EDGE,"E12.0"),sQuery(id+"F0.wireOp",EDGE,"E12.1"),sQuery(id+"F0.wireOp",EDGE,"E12.2"),sQuery(id+"F0.wireOp",EDGE,"E12.3"),sQuery(id+"F0.wireOp",EDGE,"E12.4"),sQuery(id+"F0.wireOp",EDGE,"E12.5"),sQuery(id+"F0.wireOp",EDGE,"E12.6"),sQuery(id+"F0.wireOp",EDGE,"E12.7"),sQuery(id+"F0.wireOp",EDGE,"E12.8"),sQuery(id+"F0.wireOp",EDGE,"E12.9"),sQuery(id+"F0.wireOp",EDGE,"E12.10"),sQuery(id+"F0.wireOp",EDGE,"E12.11")])]}),"instanceName":"1"}),"instanceName":"1"});
            booleanBodies(context, id + "F10", {"operationType" : BooleanOperationType.UNION, "tools" : qUnion([Q0, Q1, Q2])});
        }
        {
            var Q0;
            Q0=makeQuery(id+"F1.opExtrude","SWEPT_BODY",BODY,{"disambiguationData":[OSD([sQuery(id+"F0.wireOp",EDGE,"E0.bottom"),sQuery(id+"F0.wireOp",EDGE,"E0.top"),sQuery(id+"F0.wireOp",EDGE,"E1"),sQuery(id+"F0.wireOp",EDGE,"E2"),sQuery(id+"F0.wireOp",EDGE,"E3"),sQuery(id+"F0.wireOp",EDGE,"E4"),sQuery(id+"F0.wireOp",EDGE,"E5.filletArc"),sQuery(id+"F0.wireOp",EDGE,"E6.filletArc"),sQuery(id+"F0.wireOp",EDGE,"E7.filletArc"),sQuery(id+"F0.wireOp",EDGE,"E8.filletArc"),sQuery(id+"F0.wireOp",EDGE,"E9.filletArc"),sQuery(id+"F0.wireOp",EDGE,"E10.filletArc"),sQuery(id+"F0.wireOp",EDGE,"E12.0"),sQuery(id+"F0.wireOp",EDGE,"E12.1"),sQuery(id+"F0.wireOp",EDGE,"E12.2"),sQuery(id+"F0.wireOp",EDGE,"E12.3"),sQuery(id+"F0.wireOp",EDGE,"E12.4"),sQuery(id+"F0.wireOp",EDGE,"E12.5"),sQuery(id+"F0.wireOp",EDGE,"E12.6"),sQuery(id+"F0.wireOp",EDGE,"E12.7"),sQuery(id+"F0.wireOp",EDGE,"E12.8"),sQuery(id+"F0.wireOp",EDGE,"E12.9"),sQuery(id+"F0.wireOp",EDGE,"E12.10"),sQuery(id+"F0.wireOp",EDGE,"E12.11")])]});
            transform(context, id + "F11", {"entities" : qUnion([Q0]), "transformType" : TransformType.TRANSLATION_3D, "dx" : 0 * mm, "dy" : 0 * mm, "dz" : (36 * 3) * mm, "makeCopy" : true});
        }
        {
            var Q0;
            Q0=makeQuery(id+"F1.opExtrude","SWEPT_BODY",BODY,{"disambiguationData":[OSD([sQuery(id+"F0.wireOp",EDGE,"E0.bottom"),sQuery(id+"F0.wireOp",EDGE,"E0.top"),sQuery(id+"F0.wireOp",EDGE,"E1"),sQuery(id+"F0.wireOp",EDGE,"E2"),sQuery(id+"F0.wireOp",EDGE,"E3"),sQuery(id+"F0.wireOp",EDGE,"E4"),sQuery(id+"F0.wireOp",EDGE,"E5.filletArc"),sQuery(id+"F0.wireOp",EDGE,"E6.filletArc"),sQuery(id+"F0.wireOp",EDGE,"E7.filletArc"),sQuery(id+"F0.wireOp",EDGE,"E8.filletArc"),sQuery(id+"F0.wireOp",EDGE,"E9.filletArc"),sQuery(id+"F0.wireOp",EDGE,"E10.filletArc"),sQuery(id+"F0.wireOp",EDGE,"E12.0"),sQuery(id+"F0.wireOp",EDGE,"E12.1"),sQuery(id+"F0.wireOp",EDGE,"E12.2"),sQuery(id+"F0.wireOp",EDGE,"E12.3"),sQuery(id+"F0.wireOp",EDGE,"E12.4"),sQuery(id+"F0.wireOp",EDGE,"E12.5"),sQuery(id+"F0.wireOp",EDGE,"E12.6"),sQuery(id+"F0.wireOp",EDGE,"E12.7"),sQuery(id+"F0.wireOp",EDGE,"E12.8"),sQuery(id+"F0.wireOp",EDGE,"E12.9"),sQuery(id+"F0.wireOp",EDGE,"E12.10"),sQuery(id+"F0.wireOp",EDGE,"E12.11")])]});
            var Q1;
            Q1=makeQuery(id+"F11.opPattern","COPY",BODY,{"derivedFrom":makeQuery(id+"F1.opExtrude","SWEPT_BODY",BODY,{"disambiguationData":[OSD([sQuery(id+"F0.wireOp",EDGE,"E0.bottom"),sQuery(id+"F0.wireOp",EDGE,"E0.top"),sQuery(id+"F0.wireOp",EDGE,"E1"),sQuery(id+"F0.wireOp",EDGE,"E2"),sQuery(id+"F0.wireOp",EDGE,"E3"),sQuery(id+"F0.wireOp",EDGE,"E4"),sQuery(id+"F0.wireOp",EDGE,"E5.filletArc"),sQuery(id+"F0.wireOp",EDGE,"E6.filletArc"),sQuery(id+"F0.wireOp",EDGE,"E7.filletArc"),sQuery(id+"F0.wireOp",EDGE,"E8.filletArc"),sQuery(id+"F0.wireOp",EDGE,"E9.filletArc"),sQuery(id+"F0.wireOp",EDGE,"E10.filletArc"),sQuery(id+"F0.wireOp",EDGE,"E12.0"),sQuery(id+"F0.wireOp",EDGE,"E12.1"),sQuery(id+"F0.wireOp",EDGE,"E12.2"),sQuery(id+"F0.wireOp",EDGE,"E12.3"),sQuery(id+"F0.wireOp",EDGE,"E12.4"),sQuery(id+"F0.wireOp",EDGE,"E12.5"),sQuery(id+"F0.wireOp",EDGE,"E12.6"),sQuery(id+"F0.wireOp",EDGE,"E12.7"),sQuery(id+"F0.wireOp",EDGE,"E12.8"),sQuery(id+"F0.wireOp",EDGE,"E12.9"),sQuery(id+"F0.wireOp",EDGE,"E12.10"),sQuery(id+"F0.wireOp",EDGE,"E12.11")])]}),"instanceName":"1"});
            booleanBodies(context, id + "F12", {"operationType" : BooleanOperationType.UNION, "tools" : qUnion([Q0, Q1])});
        }
        {
            var Q0;
            Q0=makeQuery(id+"F1.opExtrude","SWEPT_BODY",BODY,{"disambiguationData":[OSD([sQuery(id+"F0.wireOp",EDGE,"E0.bottom"),sQuery(id+"F0.wireOp",EDGE,"E0.top"),sQuery(id+"F0.wireOp",EDGE,"E1"),sQuery(id+"F0.wireOp",EDGE,"E2"),sQuery(id+"F0.wireOp",EDGE,"E3"),sQuery(id+"F0.wireOp",EDGE,"E4"),sQuery(id+"F0.wireOp",EDGE,"E5.filletArc"),sQuery(id+"F0.wireOp",EDGE,"E6.filletArc"),sQuery(id+"F0.wireOp",EDGE,"E7.filletArc"),sQuery(id+"F0.wireOp",EDGE,"E8.filletArc"),sQuery(id+"F0.wireOp",EDGE,"E9.filletArc"),sQuery(id+"F0.wireOp",EDGE,"E10.filletArc"),sQuery(id+"F0.wireOp",EDGE,"E12.0"),sQuery(id+"F0.wireOp",EDGE,"E12.1"),sQuery(id+"F0.wireOp",EDGE,"E12.2"),sQuery(id+"F0.wireOp",EDGE,"E12.3"),sQuery(id+"F0.wireOp",EDGE,"E12.4"),sQuery(id+"F0.wireOp",EDGE,"E12.5"),sQuery(id+"F0.wireOp",EDGE,"E12.6"),sQuery(id+"F0.wireOp",EDGE,"E12.7"),sQuery(id+"F0.wireOp",EDGE,"E12.8"),sQuery(id+"F0.wireOp",EDGE,"E12.9"),sQuery(id+"F0.wireOp",EDGE,"E12.10"),sQuery(id+"F0.wireOp",EDGE,"E12.11")])]});
            transform(context, id + "F13", {"entities" : qUnion([Q0]), "transformType" : TransformType.TRANSLATION_3D, "dx" : 50.5 * mm, "dy" : 0 * mm, "dz" : 0 * mm, "makeCopy" : true});
        }
        {
            var Q0;
            Q0=makeQuery(id+"F1.opExtrude","SWEPT_BODY",BODY,{"disambiguationData":[OSD([sQuery(id+"F0.wireOp",EDGE,"E0.bottom"),sQuery(id+"F0.wireOp",EDGE,"E0.top"),sQuery(id+"F0.wireOp",EDGE,"E1"),sQuery(id+"F0.wireOp",EDGE,"E2"),sQuery(id+"F0.wireOp",EDGE,"E3"),sQuery(id+"F0.wireOp",EDGE,"E4"),sQuery(id+"F0.wireOp",EDGE,"E5.filletArc"),sQuery(id+"F0.wireOp",EDGE,"E6.filletArc"),sQuery(id+"F0.wireOp",EDGE,"E7.filletArc"),sQuery(id+"F0.wireOp",EDGE,"E8.filletArc"),sQuery(id+"F0.wireOp",EDGE,"E9.filletArc"),sQuery(id+"F0.wireOp",EDGE,"E10.filletArc"),sQuery(id+"F0.wireOp",EDGE,"E12.0"),sQuery(id+"F0.wireOp",EDGE,"E12.1"),sQuery(id+"F0.wireOp",EDGE,"E12.2"),sQuery(id+"F0.wireOp",EDGE,"E12.3"),sQuery(id+"F0.wireOp",EDGE,"E12.4"),sQuery(id+"F0.wireOp",EDGE,"E12.5"),sQuery(id+"F0.wireOp",EDGE,"E12.6"),sQuery(id+"F0.wireOp",EDGE,"E12.7"),sQuery(id+"F0.wireOp",EDGE,"E12.8"),sQuery(id+"F0.wireOp",EDGE,"E12.9"),sQuery(id+"F0.wireOp",EDGE,"E12.10"),sQuery(id+"F0.wireOp",EDGE,"E12.11")])]});
            transform(context, id + "F14", {"entities" : qUnion([Q0]), "transformType" : TransformType.TRANSLATION_3D, "dx" : 101 * mm, "dy" : 0 * mm, "dz" : 0 * mm, "makeCopy" : true});
        }
        {
            var Q0;
            Q0=makeQuery(id+"F14.opPattern","COPY",BODY,{"derivedFrom":makeQuery(id+"F1.opExtrude","SWEPT_BODY",BODY,{"disambiguationData":[OSD([sQuery(id+"F0.wireOp",EDGE,"E0.bottom"),sQuery(id+"F0.wireOp",EDGE,"E0.top"),sQuery(id+"F0.wireOp",EDGE,"E1"),sQuery(id+"F0.wireOp",EDGE,"E2"),sQuery(id+"F0.wireOp",EDGE,"E3"),sQuery(id+"F0.wireOp",EDGE,"E4"),sQuery(id+"F0.wireOp",EDGE,"E5.filletArc"),sQuery(id+"F0.wireOp",EDGE,"E6.filletArc"),sQuery(id+"F0.wireOp",EDGE,"E7.filletArc"),sQuery(id+"F0.wireOp",EDGE,"E8.filletArc"),sQuery(id+"F0.wireOp",EDGE,"E9.filletArc"),sQuery(id+"F0.wireOp",EDGE,"E10.filletArc"),sQuery(id+"F0.wireOp",EDGE,"E12.0"),sQuery(id+"F0.wireOp",EDGE,"E12.1"),sQuery(id+"F0.wireOp",EDGE,"E12.2"),sQuery(id+"F0.wireOp",EDGE,"E12.3"),sQuery(id+"F0.wireOp",EDGE,"E12.4"),sQuery(id+"F0.wireOp",EDGE,"E12.5"),sQuery(id+"F0.wireOp",EDGE,"E12.6"),sQuery(id+"F0.wireOp",EDGE,"E12.7"),sQuery(id+"F0.wireOp",EDGE,"E12.8"),sQuery(id+"F0.wireOp",EDGE,"E12.9"),sQuery(id+"F0.wireOp",EDGE,"E12.10"),sQuery(id+"F0.wireOp",EDGE,"E12.11")])]}),"instanceName":"1"});
            transform(context, id + "F15", {"entities" : qUnion([Q0]), "transformType" : TransformType.TRANSLATION_3D, "dx" : 101 * mm, "dy" : 0 * mm, "dz" : 0 * mm, "makeCopy" : true});
        }
        {
            var Q0;
            Q0=makeQuery(id+"F15.opPattern","COPY",BODY,{"derivedFrom":makeQuery(id+"F14.opPattern","COPY",BODY,{"derivedFrom":makeQuery(id+"F1.opExtrude","SWEPT_BODY",BODY,{"disambiguationData":[OSD([sQuery(id+"F0.wireOp",EDGE,"E0.bottom"),sQuery(id+"F0.wireOp",EDGE,"E0.top"),sQuery(id+"F0.wireOp",EDGE,"E1"),sQuery(id+"F0.wireOp",EDGE,"E2"),sQuery(id+"F0.wireOp",EDGE,"E3"),sQuery(id+"F0.wireOp",EDGE,"E4"),sQuery(id+"F0.wireOp",EDGE,"E5.filletArc"),sQuery(id+"F0.wireOp",EDGE,"E6.filletArc"),sQuery(id+"F0.wireOp",EDGE,"E7.filletArc"),sQuery(id+"F0.wireOp",EDGE,"E8.filletArc"),sQuery(id+"F0.wireOp",EDGE,"E9.filletArc"),sQuery(id+"F0.wireOp",EDGE,"E10.filletArc"),sQuery(id+"F0.wireOp",EDGE,"E12.0"),sQuery(id+"F0.wireOp",EDGE,"E12.1"),sQuery(id+"F0.wireOp",EDGE,"E12.2"),sQuery(id+"F0.wireOp",EDGE,"E12.3"),sQuery(id+"F0.wireOp",EDGE,"E12.4"),sQuery(id+"F0.wireOp",EDGE,"E12.5"),sQuery(id+"F0.wireOp",EDGE,"E12.6"),sQuery(id+"F0.wireOp",EDGE,"E12.7"),sQuery(id+"F0.wireOp",EDGE,"E12.8"),sQuery(id+"F0.wireOp",EDGE,"E12.9"),sQuery(id+"F0.wireOp",EDGE,"E12.10"),sQuery(id+"F0.wireOp",EDGE,"E12.11")])]}),"instanceName":"1"}),"instanceName":"1"});
            transform(context, id + "F16", {"entities" : qUnion([Q0]), "transformType" : TransformType.TRANSLATION_3D, "dx" : 101 * mm, "dy" : 0 * mm, "dz" : 0 * mm, "makeCopy" : true});
        }
        {
            var Q0;
            Q0=makeQuery(id+"F16.opPattern","COPY",BODY,{"derivedFrom":makeQuery(id+"F15.opPattern","COPY",BODY,{"derivedFrom":makeQuery(id+"F14.opPattern","COPY",BODY,{"derivedFrom":makeQuery(id+"F1.opExtrude","SWEPT_BODY",BODY,{"disambiguationData":[OSD([sQuery(id+"F0.wireOp",EDGE,"E0.bottom"),sQuery(id+"F0.wireOp",EDGE,"E0.top"),sQuery(id+"F0.wireOp",EDGE,"E1"),sQuery(id+"F0.wireOp",EDGE,"E2"),sQuery(id+"F0.wireOp",EDGE,"E3"),sQuery(id+"F0.wireOp",EDGE,"E4"),sQuery(id+"F0.wireOp",EDGE,"E5.filletArc"),sQuery(id+"F0.wireOp",EDGE,"E6.filletArc"),sQuery(id+"F0.wireOp",EDGE,"E7.filletArc"),sQuery(id+"F0.wireOp",EDGE,"E8.filletArc"),sQuery(id+"F0.wireOp",EDGE,"E9.filletArc"),sQuery(id+"F0.wireOp",EDGE,"E10.filletArc"),sQuery(id+"F0.wireOp",EDGE,"E12.0"),sQuery(id+"F0.wireOp",EDGE,"E12.1"),sQuery(id+"F0.wireOp",EDGE,"E12.2"),sQuery(id+"F0.wireOp",EDGE,"E12.3"),sQuery(id+"F0.wireOp",EDGE,"E12.4"),sQuery(id+"F0.wireOp",EDGE,"E12.5"),sQuery(id+"F0.wireOp",EDGE,"E12.6"),sQuery(id+"F0.wireOp",EDGE,"E12.7"),sQuery(id+"F0.wireOp",EDGE,"E12.8"),sQuery(id+"F0.wireOp",EDGE,"E12.9"),sQuery(id+"F0.wireOp",EDGE,"E12.10"),sQuery(id+"F0.wireOp",EDGE,"E12.11")])]}),"instanceName":"1"}),"instanceName":"1"}),"instanceName":"1"});
            transform(context, id + "F17", {"entities" : qUnion([Q0]), "transformType" : TransformType.TRANSLATION_3D, "dx" : 101 * mm, "dy" : 0 * mm, "dz" : 0 * mm, "makeCopy" : true});
        }
        {
            var Q0;
            Q0=makeQuery(id+"F17.opPattern","COPY",BODY,{"derivedFrom":makeQuery(id+"F16.opPattern","COPY",BODY,{"derivedFrom":makeQuery(id+"F15.opPattern","COPY",BODY,{"derivedFrom":makeQuery(id+"F14.opPattern","COPY",BODY,{"derivedFrom":makeQuery(id+"F1.opExtrude","SWEPT_BODY",BODY,{"disambiguationData":[OSD([sQuery(id+"F0.wireOp",EDGE,"E0.bottom"),sQuery(id+"F0.wireOp",EDGE,"E0.top"),sQuery(id+"F0.wireOp",EDGE,"E1"),sQuery(id+"F0.wireOp",EDGE,"E2"),sQuery(id+"F0.wireOp",EDGE,"E3"),sQuery(id+"F0.wireOp",EDGE,"E4"),sQuery(id+"F0.wireOp",EDGE,"E5.filletArc"),sQuery(id+"F0.wireOp",EDGE,"E6.filletArc"),sQuery(id+"F0.wireOp",EDGE,"E7.filletArc"),sQuery(id+"F0.wireOp",EDGE,"E8.filletArc"),sQuery(id+"F0.wireOp",EDGE,"E9.filletArc"),sQuery(id+"F0.wireOp",EDGE,"E10.filletArc"),sQuery(id+"F0.wireOp",EDGE,"E12.0"),sQuery(id+"F0.wireOp",EDGE,"E12.1"),sQuery(id+"F0.wireOp",EDGE,"E12.2"),sQuery(id+"F0.wireOp",EDGE,"E12.3"),sQuery(id+"F0.wireOp",EDGE,"E12.4"),sQuery(id+"F0.wireOp",EDGE,"E12.5"),sQuery(id+"F0.wireOp",EDGE,"E12.6"),sQuery(id+"F0.wireOp",EDGE,"E12.7"),sQuery(id+"F0.wireOp",EDGE,"E12.8"),sQuery(id+"F0.wireOp",EDGE,"E12.9"),sQuery(id+"F0.wireOp",EDGE,"E12.10"),sQuery(id+"F0.wireOp",EDGE,"E12.11")])]}),"instanceName":"1"}),"instanceName":"1"}),"instanceName":"1"}),"instanceName":"1"});
            transform(context, id + "F18", {"entities" : qUnion([Q0]), "transformType" : TransformType.TRANSLATION_3D, "dx" : 101 * mm, "dy" : 0 * mm, "dz" : 0 * mm, "makeCopy" : true});
        }
        {
            var Q0;
            Q0=makeQuery(id+"F18.opPattern","COPY",BODY,{"derivedFrom":makeQuery(id+"F17.opPattern","COPY",BODY,{"derivedFrom":makeQuery(id+"F16.opPattern","COPY",BODY,{"derivedFrom":makeQuery(id+"F15.opPattern","COPY",BODY,{"derivedFrom":makeQuery(id+"F14.opPattern","COPY",BODY,{"derivedFrom":makeQuery(id+"F1.opExtrude","SWEPT_BODY",BODY,{"disambiguationData":[OSD([sQuery(id+"F0.wireOp",EDGE,"E0.bottom"),sQuery(id+"F0.wireOp",EDGE,"E0.top"),sQuery(id+"F0.wireOp",EDGE,"E1"),sQuery(id+"F0.wireOp",EDGE,"E2"),sQuery(id+"F0.wireOp",EDGE,"E3"),sQuery(id+"F0.wireOp",EDGE,"E4"),sQuery(id+"F0.wireOp",EDGE,"E5.filletArc"),sQuery(id+"F0.wireOp",EDGE,"E6.filletArc"),sQuery(id+"F0.wireOp",EDGE,"E7.filletArc"),sQuery(id+"F0.wireOp",EDGE,"E8.filletArc"),sQuery(id+"F0.wireOp",EDGE,"E9.filletArc"),sQuery(id+"F0.wireOp",EDGE,"E10.filletArc"),sQuery(id+"F0.wireOp",EDGE,"E12.0"),sQuery(id+"F0.wireOp",EDGE,"E12.1"),sQuery(id+"F0.wireOp",EDGE,"E12.2"),sQuery(id+"F0.wireOp",EDGE,"E12.3"),sQuery(id+"F0.wireOp",EDGE,"E12.4"),sQuery(id+"F0.wireOp",EDGE,"E12.5"),sQuery(id+"F0.wireOp",EDGE,"E12.6"),sQuery(id+"F0.wireOp",EDGE,"E12.7"),sQuery(id+"F0.wireOp",EDGE,"E12.8"),sQuery(id+"F0.wireOp",EDGE,"E12.9"),sQuery(id+"F0.wireOp",EDGE,"E12.10"),sQuery(id+"F0.wireOp",EDGE,"E12.11")])]}),"instanceName":"1"}),"instanceName":"1"}),"instanceName":"1"}),"instanceName":"1"}),"instanceName":"1"});
            transform(context, id + "F19", {"entities" : qUnion([Q0]), "transformType" : TransformType.TRANSLATION_3D, "dx" : 101 * mm, "dy" : 0 * mm, "dz" : 0 * mm, "makeCopy" : true});
        }
        {
            var Q0;
            Q0=makeQuery(id+"F19.opPattern","COPY",BODY,{"derivedFrom":makeQuery(id+"F18.opPattern","COPY",BODY,{"derivedFrom":makeQuery(id+"F17.opPattern","COPY",BODY,{"derivedFrom":makeQuery(id+"F16.opPattern","COPY",BODY,{"derivedFrom":makeQuery(id+"F15.opPattern","COPY",BODY,{"derivedFrom":makeQuery(id+"F14.opPattern","COPY",BODY,{"derivedFrom":makeQuery(id+"F1.opExtrude","SWEPT_BODY",BODY,{"disambiguationData":[OSD([sQuery(id+"F0.wireOp",EDGE,"E0.bottom"),sQuery(id+"F0.wireOp",EDGE,"E0.top"),sQuery(id+"F0.wireOp",EDGE,"E1"),sQuery(id+"F0.wireOp",EDGE,"E2"),sQuery(id+"F0.wireOp",EDGE,"E3"),sQuery(id+"F0.wireOp",EDGE,"E4"),sQuery(id+"F0.wireOp",EDGE,"E5.filletArc"),sQuery(id+"F0.wireOp",EDGE,"E6.filletArc"),sQuery(id+"F0.wireOp",EDGE,"E7.filletArc"),sQuery(id+"F0.wireOp",EDGE,"E8.filletArc"),sQuery(id+"F0.wireOp",EDGE,"E9.filletArc"),sQuery(id+"F0.wireOp",EDGE,"E10.filletArc"),sQuery(id+"F0.wireOp",EDGE,"E12.0"),sQuery(id+"F0.wireOp",EDGE,"E12.1"),sQuery(id+"F0.wireOp",EDGE,"E12.2"),sQuery(id+"F0.wireOp",EDGE,"E12.3"),sQuery(id+"F0.wireOp",EDGE,"E12.4"),sQuery(id+"F0.wireOp",EDGE,"E12.5"),sQuery(id+"F0.wireOp",EDGE,"E12.6"),sQuery(id+"F0.wireOp",EDGE,"E12.7"),sQuery(id+"F0.wireOp",EDGE,"E12.8"),sQuery(id+"F0.wireOp",EDGE,"E12.9"),sQuery(id+"F0.wireOp",EDGE,"E12.10"),sQuery(id+"F0.wireOp",EDGE,"E12.11")])]}),"instanceName":"1"}),"instanceName":"1"}),"instanceName":"1"}),"instanceName":"1"}),"instanceName":"1"}),"instanceName":"1"});
            transform(context, id + "F20", {"entities" : qUnion([Q0]), "transformType" : TransformType.TRANSLATION_3D, "dx" : 101 * mm, "dy" : 0 * mm, "dz" : 0 * mm, "makeCopy" : true});
        }
        {
            var Q0;
            Q0=makeQuery(id+"F20.opPattern","COPY",BODY,{"derivedFrom":makeQuery(id+"F19.opPattern","COPY",BODY,{"derivedFrom":makeQuery(id+"F18.opPattern","COPY",BODY,{"derivedFrom":makeQuery(id+"F17.opPattern","COPY",BODY,{"derivedFrom":makeQuery(id+"F16.opPattern","COPY",BODY,{"derivedFrom":makeQuery(id+"F15.opPattern","COPY",BODY,{"derivedFrom":makeQuery(id+"F14.opPattern","COPY",BODY,{"derivedFrom":makeQuery(id+"F1.opExtrude","SWEPT_BODY",BODY,{"disambiguationData":[OSD([sQuery(id+"F0.wireOp",EDGE,"E0.bottom"),sQuery(id+"F0.wireOp",EDGE,"E0.top"),sQuery(id+"F0.wireOp",EDGE,"E1"),sQuery(id+"F0.wireOp",EDGE,"E2"),sQuery(id+"F0.wireOp",EDGE,"E3"),sQuery(id+"F0.wireOp",EDGE,"E4"),sQuery(id+"F0.wireOp",EDGE,"E5.filletArc"),sQuery(id+"F0.wireOp",EDGE,"E6.filletArc"),sQuery(id+"F0.wireOp",EDGE,"E7.filletArc"),sQuery(id+"F0.wireOp",EDGE,"E8.filletArc"),sQuery(id+"F0.wireOp",EDGE,"E9.filletArc"),sQuery(id+"F0.wireOp",EDGE,"E10.filletArc"),sQuery(id+"F0.wireOp",EDGE,"E12.0"),sQuery(id+"F0.wireOp",EDGE,"E12.1"),sQuery(id+"F0.wireOp",EDGE,"E12.2"),sQuery(id+"F0.wireOp",EDGE,"E12.3"),sQuery(id+"F0.wireOp",EDGE,"E12.4"),sQuery(id+"F0.wireOp",EDGE,"E12.5"),sQuery(id+"F0.wireOp",EDGE,"E12.6"),sQuery(id+"F0.wireOp",EDGE,"E12.7"),sQuery(id+"F0.wireOp",EDGE,"E12.8"),sQuery(id+"F0.wireOp",EDGE,"E12.9"),sQuery(id+"F0.wireOp",EDGE,"E12.10"),sQuery(id+"F0.wireOp",EDGE,"E12.11")])]}),"instanceName":"1"}),"instanceName":"1"}),"instanceName":"1"}),"instanceName":"1"}),"instanceName":"1"}),"instanceName":"1"}),"instanceName":"1"});
            transform(context, id + "F21", {"entities" : qUnion([Q0]), "transformType" : TransformType.TRANSLATION_3D, "dx" : 101 * mm, "dy" : 0 * mm, "dz" : 0 * mm, "makeCopy" : true});
        }
        {
            var Q0;
            Q0=makeQuery(id+"F21.opPattern","COPY",BODY,{"derivedFrom":makeQuery(id+"F20.opPattern","COPY",BODY,{"derivedFrom":makeQuery(id+"F19.opPattern","COPY",BODY,{"derivedFrom":makeQuery(id+"F18.opPattern","COPY",BODY,{"derivedFrom":makeQuery(id+"F17.opPattern","COPY",BODY,{"derivedFrom":makeQuery(id+"F16.opPattern","COPY",BODY,{"derivedFrom":makeQuery(id+"F15.opPattern","COPY",BODY,{"derivedFrom":makeQuery(id+"F14.opPattern","COPY",BODY,{"derivedFrom":makeQuery(id+"F1.opExtrude","SWEPT_BODY",BODY,{"disambiguationData":[OSD([sQuery(id+"F0.wireOp",EDGE,"E0.bottom"),sQuery(id+"F0.wireOp",EDGE,"E0.top"),sQuery(id+"F0.wireOp",EDGE,"E1"),sQuery(id+"F0.wireOp",EDGE,"E2"),sQuery(id+"F0.wireOp",EDGE,"E3"),sQuery(id+"F0.wireOp",EDGE,"E4"),sQuery(id+"F0.wireOp",EDGE,"E5.filletArc"),sQuery(id+"F0.wireOp",EDGE,"E6.filletArc"),sQuery(id+"F0.wireOp",EDGE,"E7.filletArc"),sQuery(id+"F0.wireOp",EDGE,"E8.filletArc"),sQuery(id+"F0.wireOp",EDGE,"E9.filletArc"),sQuery(id+"F0.wireOp",EDGE,"E10.filletArc"),sQuery(id+"F0.wireOp",EDGE,"E12.0"),sQuery(id+"F0.wireOp",EDGE,"E12.1"),sQuery(id+"F0.wireOp",EDGE,"E12.2"),sQuery(id+"F0.wireOp",EDGE,"E12.3"),sQuery(id+"F0.wireOp",EDGE,"E12.4"),sQuery(id+"F0.wireOp",EDGE,"E12.5"),sQuery(id+"F0.wireOp",EDGE,"E12.6"),sQuery(id+"F0.wireOp",EDGE,"E12.7"),sQuery(id+"F0.wireOp",EDGE,"E12.8"),sQuery(id+"F0.wireOp",EDGE,"E12.9"),sQuery(id+"F0.wireOp",EDGE,"E12.10"),sQuery(id+"F0.wireOp",EDGE,"E12.11")])]}),"instanceName":"1"}),"instanceName":"1"}),"instanceName":"1"}),"instanceName":"1"}),"instanceName":"1"}),"instanceName":"1"}),"instanceName":"1"}),"instanceName":"1"});
            transform(context, id + "F22", {"entities" : qUnion([Q0]), "transformType" : TransformType.TRANSLATION_3D, "dx" : 101 * mm, "dy" : 0 * mm, "dz" : 0 * mm, "makeCopy" : true});
        }
        {
            var Q0;
            Q0=makeQuery(id+"F22.opPattern","COPY",BODY,{"derivedFrom":makeQuery(id+"F21.opPattern","COPY",BODY,{"derivedFrom":makeQuery(id+"F20.opPattern","COPY",BODY,{"derivedFrom":makeQuery(id+"F19.opPattern","COPY",BODY,{"derivedFrom":makeQuery(id+"F18.opPattern","COPY",BODY,{"derivedFrom":makeQuery(id+"F17.opPattern","COPY",BODY,{"derivedFrom":makeQuery(id+"F16.opPattern","COPY",BODY,{"derivedFrom":makeQuery(id+"F15.opPattern","COPY",BODY,{"derivedFrom":makeQuery(id+"F14.opPattern","COPY",BODY,{"derivedFrom":makeQuery(id+"F1.opExtrude","SWEPT_BODY",BODY,{"disambiguationData":[OSD([sQuery(id+"F0.wireOp",EDGE,"E0.bottom"),sQuery(id+"F0.wireOp",EDGE,"E0.top"),sQuery(id+"F0.wireOp",EDGE,"E1"),sQuery(id+"F0.wireOp",EDGE,"E2"),sQuery(id+"F0.wireOp",EDGE,"E3"),sQuery(id+"F0.wireOp",EDGE,"E4"),sQuery(id+"F0.wireOp",EDGE,"E5.filletArc"),sQuery(id+"F0.wireOp",EDGE,"E6.filletArc"),sQuery(id+"F0.wireOp",EDGE,"E7.filletArc"),sQuery(id+"F0.wireOp",EDGE,"E8.filletArc"),sQuery(id+"F0.wireOp",EDGE,"E9.filletArc"),sQuery(id+"F0.wireOp",EDGE,"E10.filletArc"),sQuery(id+"F0.wireOp",EDGE,"E12.0"),sQuery(id+"F0.wireOp",EDGE,"E12.1"),sQuery(id+"F0.wireOp",EDGE,"E12.2"),sQuery(id+"F0.wireOp",EDGE,"E12.3"),sQuery(id+"F0.wireOp",EDGE,"E12.4"),sQuery(id+"F0.wireOp",EDGE,"E12.5"),sQuery(id+"F0.wireOp",EDGE,"E12.6"),sQuery(id+"F0.wireOp",EDGE,"E12.7"),sQuery(id+"F0.wireOp",EDGE,"E12.8"),sQuery(id+"F0.wireOp",EDGE,"E12.9"),sQuery(id+"F0.wireOp",EDGE,"E12.10"),sQuery(id+"F0.wireOp",EDGE,"E12.11")])]}),"instanceName":"1"}),"instanceName":"1"}),"instanceName":"1"}),"instanceName":"1"}),"instanceName":"1"}),"instanceName":"1"}),"instanceName":"1"}),"instanceName":"1"}),"instanceName":"1"});
            transform(context, id + "F23", {"entities" : qUnion([Q0]), "transformType" : TransformType.TRANSLATION_3D, "dx" : 101 * mm, "dy" : 0 * mm, "dz" : 0 * mm, "makeCopy" : true});
        }
        {
            var Q0;
            Q0=makeQuery(id+"F23.opPattern","COPY",BODY,{"derivedFrom":makeQuery(id+"F22.opPattern","COPY",BODY,{"derivedFrom":makeQuery(id+"F21.opPattern","COPY",BODY,{"derivedFrom":makeQuery(id+"F20.opPattern","COPY",BODY,{"derivedFrom":makeQuery(id+"F19.opPattern","COPY",BODY,{"derivedFrom":makeQuery(id+"F18.opPattern","COPY",BODY,{"derivedFrom":makeQuery(id+"F17.opPattern","COPY",BODY,{"derivedFrom":makeQuery(id+"F16.opPattern","COPY",BODY,{"derivedFrom":makeQuery(id+"F15.opPattern","COPY",BODY,{"derivedFrom":makeQuery(id+"F14.opPattern","COPY",BODY,{"derivedFrom":makeQuery(id+"F1.opExtrude","SWEPT_BODY",BODY,{"disambiguationData":[OSD([sQuery(id+"F0.wireOp",EDGE,"E0.bottom"),sQuery(id+"F0.wireOp",EDGE,"E0.top"),sQuery(id+"F0.wireOp",EDGE,"E1"),sQuery(id+"F0.wireOp",EDGE,"E2"),sQuery(id+"F0.wireOp",EDGE,"E3"),sQuery(id+"F0.wireOp",EDGE,"E4"),sQuery(id+"F0.wireOp",EDGE,"E5.filletArc"),sQuery(id+"F0.wireOp",EDGE,"E6.filletArc"),sQuery(id+"F0.wireOp",EDGE,"E7.filletArc"),sQuery(id+"F0.wireOp",EDGE,"E8.filletArc"),sQuery(id+"F0.wireOp",EDGE,"E9.filletArc"),sQuery(id+"F0.wireOp",EDGE,"E10.filletArc"),sQuery(id+"F0.wireOp",EDGE,"E12.0"),sQuery(id+"F0.wireOp",EDGE,"E12.1"),sQuery(id+"F0.wireOp",EDGE,"E12.2"),sQuery(id+"F0.wireOp",EDGE,"E12.3"),sQuery(id+"F0.wireOp",EDGE,"E12.4"),sQuery(id+"F0.wireOp",EDGE,"E12.5"),sQuery(id+"F0.wireOp",EDGE,"E12.6"),sQuery(id+"F0.wireOp",EDGE,"E12.7"),sQuery(id+"F0.wireOp",EDGE,"E12.8"),sQuery(id+"F0.wireOp",EDGE,"E12.9"),sQuery(id+"F0.wireOp",EDGE,"E12.10"),sQuery(id+"F0.wireOp",EDGE,"E12.11")])]}),"instanceName":"1"}),"instanceName":"1"}),"instanceName":"1"}),"instanceName":"1"}),"instanceName":"1"}),"instanceName":"1"}),"instanceName":"1"}),"instanceName":"1"}),"instanceName":"1"}),"instanceName":"1"});
            transform(context, id + "F24", {"entities" : qUnion([Q0]), "transformType" : TransformType.TRANSLATION_3D, "dx" : 101 * mm, "dy" : 0 * mm, "dz" : 0 * mm, "makeCopy" : true});
        }
        {
            var Q0;
            Q0=makeQuery(id+"F24.opPattern","COPY",BODY,{"derivedFrom":makeQuery(id+"F23.opPattern","COPY",BODY,{"derivedFrom":makeQuery(id+"F22.opPattern","COPY",BODY,{"derivedFrom":makeQuery(id+"F21.opPattern","COPY",BODY,{"derivedFrom":makeQuery(id+"F20.opPattern","COPY",BODY,{"derivedFrom":makeQuery(id+"F19.opPattern","COPY",BODY,{"derivedFrom":makeQuery(id+"F18.opPattern","COPY",BODY,{"derivedFrom":makeQuery(id+"F17.opPattern","COPY",BODY,{"derivedFrom":makeQuery(id+"F16.opPattern","COPY",BODY,{"derivedFrom":makeQuery(id+"F15.opPattern","COPY",BODY,{"derivedFrom":makeQuery(id+"F14.opPattern","COPY",BODY,{"derivedFrom":makeQuery(id+"F1.opExtrude","SWEPT_BODY",BODY,{"disambiguationData":[OSD([sQuery(id+"F0.wireOp",EDGE,"E0.bottom"),sQuery(id+"F0.wireOp",EDGE,"E0.top"),sQuery(id+"F0.wireOp",EDGE,"E1"),sQuery(id+"F0.wireOp",EDGE,"E2"),sQuery(id+"F0.wireOp",EDGE,"E3"),sQuery(id+"F0.wireOp",EDGE,"E4"),sQuery(id+"F0.wireOp",EDGE,"E5.filletArc"),sQuery(id+"F0.wireOp",EDGE,"E6.filletArc"),sQuery(id+"F0.wireOp",EDGE,"E7.filletArc"),sQuery(id+"F0.wireOp",EDGE,"E8.filletArc"),sQuery(id+"F0.wireOp",EDGE,"E9.filletArc"),sQuery(id+"F0.wireOp",EDGE,"E10.filletArc"),sQuery(id+"F0.wireOp",EDGE,"E12.0"),sQuery(id+"F0.wireOp",EDGE,"E12.1"),sQuery(id+"F0.wireOp",EDGE,"E12.2"),sQuery(id+"F0.wireOp",EDGE,"E12.3"),sQuery(id+"F0.wireOp",EDGE,"E12.4"),sQuery(id+"F0.wireOp",EDGE,"E12.5"),sQuery(id+"F0.wireOp",EDGE,"E12.6"),sQuery(id+"F0.wireOp",EDGE,"E12.7"),sQuery(id+"F0.wireOp",EDGE,"E12.8"),sQuery(id+"F0.wireOp",EDGE,"E12.9"),sQuery(id+"F0.wireOp",EDGE,"E12.10"),sQuery(id+"F0.wireOp",EDGE,"E12.11")])]}),"instanceName":"1"}),"instanceName":"1"}),"instanceName":"1"}),"instanceName":"1"}),"instanceName":"1"}),"instanceName":"1"}),"instanceName":"1"}),"instanceName":"1"}),"instanceName":"1"}),"instanceName":"1"}),"instanceName":"1"});
            transform(context, id + "F25", {"entities" : qUnion([Q0]), "transformType" : TransformType.TRANSLATION_3D, "dx" : 101 * mm, "dy" : 0 * mm, "dz" : 0 * mm, "makeCopy" : true});
        }
        {
            var Q0;
            Q0=qCreatedBy(makeId("Front.planeOp"),FACE);
            var sketch = newSketch(context, id + "F26", { "sketchPlane" : qUnion([Q0])});
            skLineSegment(sketch, "E69.bottom", {"start": v(25, 162) * mm, "end": v(1265, 162) * mm});
            skLineSegment(sketch, "E69.top", {"start": v(75, 0) * mm, "end": v(1215, 0) * mm});
            skLineSegment(sketch, "E69.left", {"start": v(0, 137) * mm, "end": v(0, 75) * mm});
            skLineSegment(sketch, "E69.right", {"start": v(1290, 137) * mm, "end": v(1290, 75) * mm});
            skPoint(sketch, "E70.visualSharp", {"position": v(0, 162) * mm});
            skArc(sketch, "E70.filletArc", {"start": v(25, 162) * mm, "mid": v(7.32, 154.68) * mm, "end": v(0, 137) * mm});
            skPoint(sketch, "E71.visualSharp", {"position": v(1290, 162) * mm});
            skArc(sketch, "E71.filletArc", {"start": v(1290, 137) * mm, "mid": v(1282.68, 154.68) * mm, "end": v(1265, 162) * mm});
            skPoint(sketch, "E72.visualSharp", {"position": v(1290, 0) * mm});
            skArc(sketch, "E72.filletArc", {"start": v(1215, 0) * mm, "mid": v(1268.03, 21.97) * mm, "end": v(1290, 75) * mm});
            skPoint(sketch, "E73.visualSharp", {"position": v(0, 0) * mm});
            skArc(sketch, "E73.filletArc", {"start": v(0, 75) * mm, "mid": v(21.97, 21.97) * mm, "end": v(75, 0) * mm});
            skLineSegment(sketch, "E74.bottom", {"start": v(-162.72, 294.3) * mm, "end": v(1413.34, 294.3) * mm});
            skLineSegment(sketch, "E74.top", {"start": v(-162.72, -207.3) * mm, "end": v(1413.34, -207.3) * mm});
            skLineSegment(sketch, "E74.left", {"start": v(-162.72, 294.3) * mm, "end": v(-162.72, -207.3) * mm});
            skLineSegment(sketch, "E74.right", {"start": v(1413.34, 294.3) * mm, "end": v(1413.34, -207.3) * mm});
            skSolve(sketch);
        }
        {
            var Q0;
            Q0 = qSketchRegion(id + "F26", true);
            extrude(context, id + "F27", {"entities" : qUnion([Q0]), "operationType" : NewBodyOperationType.REMOVE, "depth" : 25 * mm, "offsetDistance" : 25 * mm});
        }
        {
            var Q0;
            Q0=qCreatedBy(makeId("Front.planeOp"),FACE);
            var sketch = newSketch(context, id + "F28", { "sketchPlane" : qUnion([Q0])});
            skLineSegment(sketch, "E75.bottom", {"start": v(25, 162) * mm, "end": v(1265, 162) * mm});
            skLineSegment(sketch, "E75.top", {"start": v(75, 0) * mm, "end": v(1215, 0) * mm});
            skLineSegment(sketch, "E75.left", {"start": v(0, 137) * mm, "end": v(0, 75) * mm});
            skLineSegment(sketch, "E75.right", {"start": v(1290, 137) * mm, "end": v(1290, 75) * mm});
            skPoint(sketch, "E76.visualSharp", {"position": v(0, 162) * mm});
            skArc(sketch, "E76.filletArc", {"start": v(25, 162) * mm, "mid": v(7.32, 154.68) * mm, "end": v(0, 137) * mm});
            skPoint(sketch, "E77.visualSharp", {"position": v(1290, 162) * mm});
            skArc(sketch, "E77.filletArc", {"start": v(1290, 137) * mm, "mid": v(1282.68, 154.68) * mm, "end": v(1265, 162) * mm});
            skPoint(sketch, "E78.visualSharp", {"position": v(1290, 0) * mm});
            skArc(sketch, "E78.filletArc", {"start": v(1215, 0) * mm, "mid": v(1268.03, 21.97) * mm, "end": v(1290, 75) * mm});
            skPoint(sketch, "E79.visualSharp", {"position": v(0, 0) * mm});
            skArc(sketch, "E79.filletArc", {"start": v(0, 75) * mm, "mid": v(21.97, 21.97) * mm, "end": v(75, 0) * mm});
            skArc(sketch, "E80.0", {"start": v(25, 152) * mm, "mid": v(14.4, 147.6) * mm, "end": v(10, 137) * mm});
            skLineSegment(sketch, "E80.1", {"start": v(10, 137) * mm, "end": v(10, 75) * mm});
            skLineSegment(sketch, "E80.2", {"start": v(25, 152) * mm, "end": v(1265, 152) * mm});
            skArc(sketch, "E80.3", {"start": v(10, 75) * mm, "mid": v(29.04, 29.04) * mm, "end": v(75, 10) * mm});
            skArc(sketch, "E80.4", {"start": v(1280, 137) * mm, "mid": v(1275.6, 147.6) * mm, "end": v(1265, 152) * mm});
            skLineSegment(sketch, "E80.5", {"start": v(1280, 137) * mm, "end": v(1280, 75) * mm});
            skArc(sketch, "E80.6", {"start": v(1215, 10) * mm, "mid": v(1260.96, 29.04) * mm, "end": v(1280, 75) * mm});
            skLineSegment(sketch, "E80.7", {"start": v(75, 10) * mm, "end": v(1215, 10) * mm});
            skSolve(sketch);
        }
        {
            var Q0;
            Q0 = qSketchRegion(id + "F28", true);
            extrude(context, id + "F29", {"entities" : qUnion([Q0]), "depth" : 3 * mm, "offsetDistance" : 25 * mm});
        }
    });
